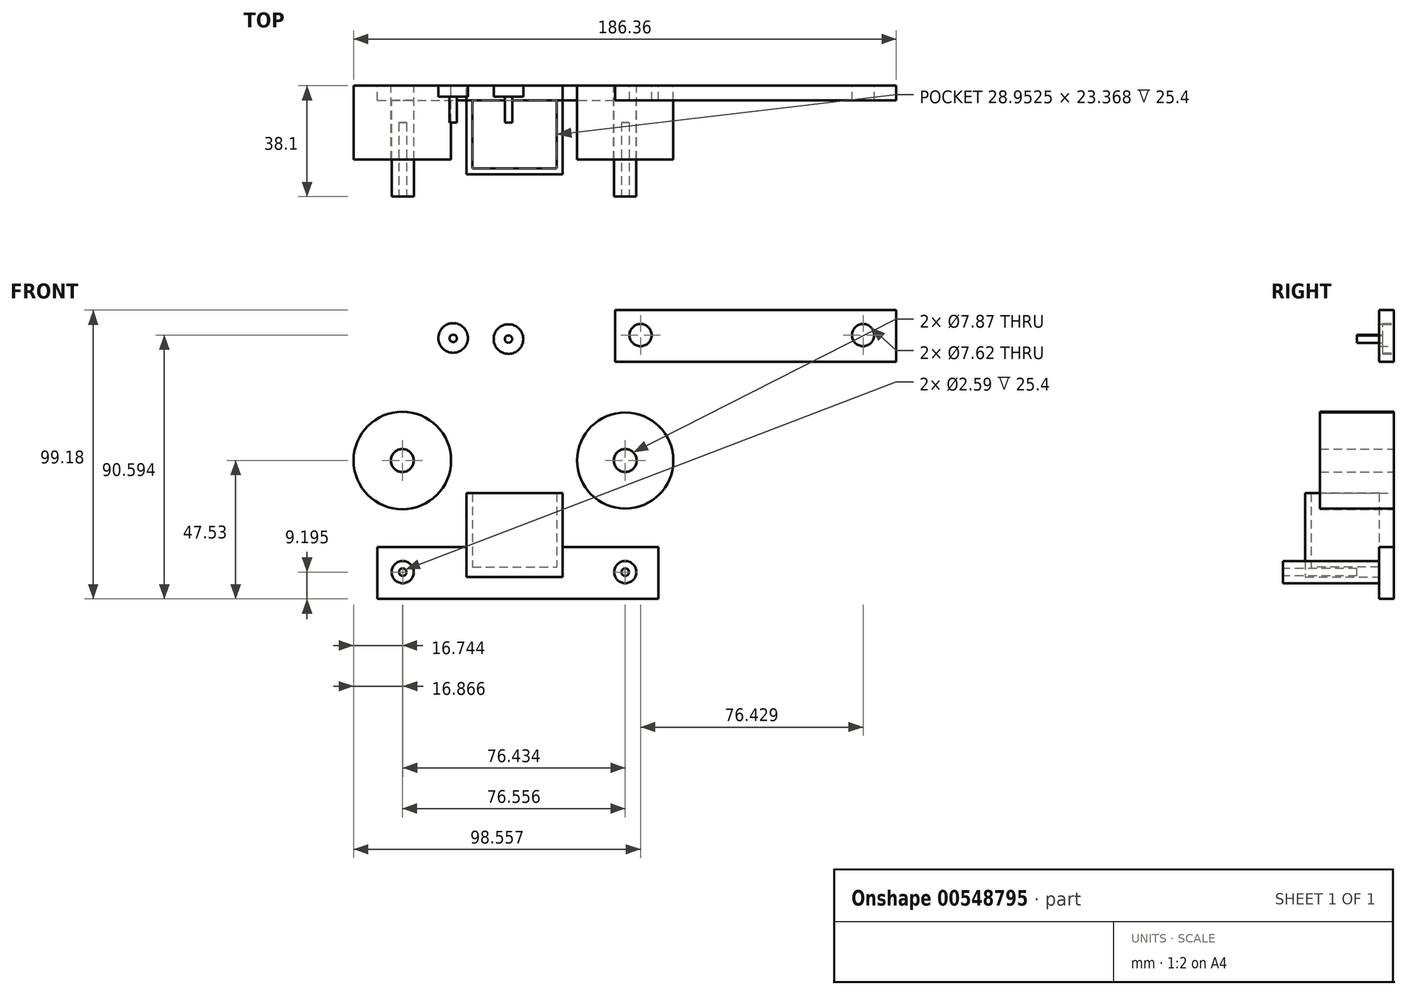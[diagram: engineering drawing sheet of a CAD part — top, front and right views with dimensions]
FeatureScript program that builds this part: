
annotation { "Feature Type Name" : "Feature", "Feature Type Description" : "" }
export const myFeature = defineFeature(function(context is Context, id is Id, definition is map)
    precondition{}
    {
        {
            var Q0;
            Q0=qCreatedBy(makeId("Front.planeOp"),FACE);
            var sketch = newSketch(context, id + "F0", { "sketchPlane" : qUnion([Q0])});
            skCircle(sketch, "E0", {"center": v(0, 0) * mm, "radius": 16.51 * mm});
            skCircle(sketch, "E1", {"center": v(0, 0) * mm, "radius": 3.94 * mm});
            skSolve(sketch);
        }
        {
            var Q0;
            Q0=makeQuery(id+"F0.imprint","IMPRINT",FACE,{"disambiguationData":[TD([[makeQuery(id+"F0.imprint","IMPRINT",EDGE,{"derivedFrom":sQuery(id+"F0.wireOp",EDGE,"E0")}),1.0]])]});
            extrude(context, id + "F1", {"entities" : qUnion([Q0]), "depth" : 25.4 * mm, "offsetDistance" : 25.4 * mm});
        }
        {
            var Q0;
            Q0=qCreatedBy(makeId("Front.planeOp"),FACE);
            var sketch = newSketch(context, id + "F2", { "sketchPlane" : qUnion([Q0])});
            skCircle(sketch, "E2", {"center": v(-76.56, 0) * mm, "radius": 16.74 * mm});
            skCircle(sketch, "E3", {"center": v(-76.56, 0) * mm, "radius": 3.94 * mm});
            skSolve(sketch);
        }
        {
            var Q0;
            Q0 = qSketchRegion(id + "F2", true);
            extrude(context, id + "F3", {"entities" : qUnion([Q0]), "depth" : 25.4 * mm, "offsetDistance" : 25.4 * mm});
        }
        {
            var Q0;
            Q0=qCreatedBy(makeId("Front.planeOp"),FACE);
            var sketch = newSketch(context, id + "F4", { "sketchPlane" : qUnion([Q0])});
            skCircle(sketch, "E4", {"center": v(0, -38.34) * mm, "radius": 3.81 * mm});
            skCircle(sketch, "E5", {"center": v(-76.43, -38.34) * mm, "radius": 3.81 * mm});
            skSolve(sketch);
        }
        {
            var Q0;
            Q0=qCreatedBy(makeId("Front.planeOp"),FACE);
            var sketch = newSketch(context, id + "F5", { "sketchPlane" : qUnion([Q0])});
            skLineSegment(sketch, "E6.bottom", {"start": v(-85.14, -29.75) * mm, "end": v(11.38, -29.75) * mm});
            skLineSegment(sketch, "E6.top", {"start": v(-85.14, -47.53) * mm, "end": v(11.38, -47.53) * mm});
            skLineSegment(sketch, "E6.left", {"start": v(-85.14, -29.75) * mm, "end": v(-85.14, -47.53) * mm});
            skLineSegment(sketch, "E6.right", {"start": v(11.38, -29.75) * mm, "end": v(11.38, -47.53) * mm});
            skSolve(sketch);
        }
        {
            var Q0;
            Q0=makeQuery(id+"F5.imprint","IMPRINT",FACE,{"disambiguationData":[TD([[makeQuery(id+"F5.imprint","IMPRINT",EDGE,{"derivedFrom":sQuery(id+"F5.wireOp",EDGE,"E6.bottom")}),-1.0]])]});
            extrude(context, id + "F6", {"entities" : qUnion([Q0]), "depth" : 5.08 * mm, "offsetDistance" : 25.4 * mm});
        }
        {
            var Q0;
            Q0=makeQuery(id+"F4.imprint","IMPRINT",FACE,{"disambiguationData":[TD([[makeQuery(id+"F4.imprint","IMPRINT",EDGE,{"derivedFrom":sQuery(id+"F4.wireOp",EDGE,"E4")}),1.0]])]});
            extrude(context, id + "F7", {"entities" : qUnion([Q0]), "operationType" : NewBodyOperationType.ADD, "depth" : 38.1 * mm, "offsetDistance" : 25.4 * mm});
        }
        {
            var Q0;
            Q0=makeQuery(id+"F4.imprint","IMPRINT",FACE,{"disambiguationData":[TD([[makeQuery(id+"F4.imprint","IMPRINT",EDGE,{"derivedFrom":sQuery(id+"F4.wireOp",EDGE,"E5")}),1.0]])]});
            extrude(context, id + "F8", {"entities" : qUnion([Q0]), "operationType" : NewBodyOperationType.ADD, "depth" : 38.1 * mm, "offsetDistance" : 25.4 * mm});
        }
        {
            var Q0;
            Q0=qCreatedBy(makeId("Front.planeOp"),FACE);
            var sketch = newSketch(context, id + "F9", { "sketchPlane" : qUnion([Q0])});
            skLineSegment(sketch, "E7.bottom", {"start": v(-3.46, 51.65) * mm, "end": v(93.06, 51.65) * mm});
            skLineSegment(sketch, "E7.top", {"start": v(-3.46, 33.87) * mm, "end": v(93.06, 33.87) * mm});
            skLineSegment(sketch, "E7.left", {"start": v(-3.46, 51.65) * mm, "end": v(-3.46, 33.87) * mm});
            skLineSegment(sketch, "E7.right", {"start": v(93.06, 51.65) * mm, "end": v(93.06, 33.87) * mm});
            skCircle(sketch, "E8", {"center": v(5.26, 43.06) * mm, "radius": 3.81 * mm});
            skCircle(sketch, "E9", {"center": v(81.69, 43.06) * mm, "radius": 3.81 * mm});
            skSolve(sketch);
        }
        {
            var Q0;
            Q0=makeQuery(id+"F9.imprint","IMPRINT",FACE,{"disambiguationData":[TD([[makeQuery(id+"F9.imprint","IMPRINT",EDGE,{"derivedFrom":sQuery(id+"F9.wireOp",EDGE,"E7.bottom")}),-1.0]])]});
            extrude(context, id + "F10", {"entities" : qUnion([Q0]), "depth" : 5.08 * mm, "offsetDistance" : 25.4 * mm});
        }
        {
            var Q0;
            Q0=qCreatedBy(makeId("Front.planeOp"),FACE);
            var sketch = newSketch(context, id + "F11", { "sketchPlane" : qUnion([Q0])});
            skCircle(sketch, "E10", {"center": v(-59.08, 41.95) * mm, "radius": 1.27 * mm});
            skSolve(sketch);
        }
        {
            var Q0;
            Q0 = qSketchRegion(id + "F11", true);
            extrude(context, id + "F12", {"entities" : qUnion([Q0]), "depth" : 12.7 * mm, "offsetDistance" : 25.4 * mm});
        }
        {
            var Q0;
            Q0=qCreatedBy(makeId("Front.planeOp"),FACE);
            var sketch = newSketch(context, id + "F13", { "sketchPlane" : qUnion([Q0])});
            skCircle(sketch, "E11", {"center": v(-59.12, 42.07) * mm, "radius": 5.08 * mm});
            skSolve(sketch);
        }
        {
            var Q0;
            Q0 = qSketchRegion(id + "F13", true);
            extrude(context, id + "F14", {"entities" : qUnion([Q0]), "operationType" : NewBodyOperationType.ADD, "depth" : 3.8 * mm, "offsetDistance" : 25.4 * mm});
        }
        {
            var Q0;
            Q0=makeQuery(id+"F6.opExtrude","CAP_FACE",FACE,{"disambiguationData":[OSD([sQuery(id+"F5.wireOp",EDGE,"E6.bottom"),sQuery(id+"F5.wireOp",EDGE,"E6.top"),sQuery(id+"F5.wireOp",EDGE,"E6.left"),sQuery(id+"F5.wireOp",EDGE,"E6.right")])],"isStart":false});
            var sketch = newSketch(context, id + "F15", { "sketchPlane" : qUnion([Q0])});
            skLineSegment(sketch, "E12.bottom", {"start": v(-54.5, -36.63) * mm, "end": v(-21.5, -36.63) * mm});
            skLineSegment(sketch, "E12.top", {"start": v(-54.5, -39.95) * mm, "end": v(-21.5, -39.95) * mm});
            skLineSegment(sketch, "E12.left", {"start": v(-54.5, -36.63) * mm, "end": v(-54.5, -39.95) * mm});
            skLineSegment(sketch, "E12.right", {"start": v(-21.5, -36.63) * mm, "end": v(-21.5, -39.95) * mm});
            skSolve(sketch);
        }
        {
            var Q0;
            Q0=makeQuery(id+"F15.imprint","IMPRINT",FACE,{"disambiguationData":[TD([[makeQuery(id+"F15.imprint","IMPRINT",EDGE,{"derivedFrom":sQuery(id+"F15.wireOp",EDGE,"E12.bottom")}),-1.0]])]});
            extrude(context, id + "F16", {"entities" : qUnion([Q0]), "operationType" : NewBodyOperationType.ADD, "depth" : 25.4 * mm, "offsetDistance" : 25.4 * mm});
        }
        {
            var Q0;
            Q0=makeQuery(id+"F8.opExtrude","CAP_FACE",FACE,{"disambiguationData":[OSD([sQuery(id+"F4.wireOp",EDGE,"E5")])],"isStart":false});
            var sketch = newSketch(context, id + "F17", { "sketchPlane" : qUnion([Q0])});
            skCircle(sketch, "E13", {"center": v(-76.43, -38.34) * mm, "radius": 1.3 * mm});
            skSolve(sketch);
        }
        {
            var Q0;
            Q0=makeQuery(id+"F17.imprint","IMPRINT",FACE,{"disambiguationData":[TD([[makeQuery(id+"F17.imprint","IMPRINT",EDGE,{"derivedFrom":sQuery(id+"F17.wireOp",EDGE,"E13")}),1.0]])]});
            extrude(context, id + "F18", {"entities" : qUnion([Q0]), "operationType" : NewBodyOperationType.REMOVE, "oppositeDirection" : true, "depth" : 25.4 * mm, "offsetDistance" : 25.4 * mm});
        }
        {
            var Q0;
            Q0=makeQuery(id+"F7.opExtrude","CAP_FACE",FACE,{"disambiguationData":[OSD([sQuery(id+"F4.wireOp",EDGE,"E4")])],"isStart":false});
            var sketch = newSketch(context, id + "F19", { "sketchPlane" : qUnion([Q0])});
            skCircle(sketch, "E14", {"center": v(0, -38.34) * mm, "radius": 1.3 * mm});
            skSolve(sketch);
        }
        {
            var Q0;
            Q0=makeQuery(id+"F19.imprint","IMPRINT",FACE,{"disambiguationData":[TD([[makeQuery(id+"F19.imprint","IMPRINT",EDGE,{"derivedFrom":sQuery(id+"F19.wireOp",EDGE,"E14")}),1.0]])]});
            extrude(context, id + "F20", {"entities" : qUnion([Q0]), "operationType" : NewBodyOperationType.REMOVE, "oppositeDirection" : true, "depth" : 25.4 * mm, "offsetDistance" : 25.4 * mm});
        }
        {
            var Q0;
            Q0=makeQuery(id+"F16.opExtrude","SWEPT_FACE",FACE,{"disambiguationData":[OSD([sQuery(id+"F15.wireOp",EDGE,"E12.bottom")])]});
            var sketch = newSketch(context, id + "F21", { "sketchPlane" : qUnion([Q0])});
            skLineSegment(sketch, "E15.bottom", {"start": v(-54.5, -5.08) * mm, "end": v(-52.48, -5.08) * mm});
            skLineSegment(sketch, "E15.top", {"start": v(-54.5, -30.48) * mm, "end": v(-52.48, -30.48) * mm});
            skLineSegment(sketch, "E15.left", {"start": v(-54.5, -5.08) * mm, "end": v(-54.5, -30.48) * mm});
            skLineSegment(sketch, "E15.right", {"start": v(-52.48, -5.08) * mm, "end": v(-52.48, -30.48) * mm});
            skLineSegment(sketch, "E16.bottom", {"start": v(-21.5, -30.48) * mm, "end": v(-23.53, -30.48) * mm});
            skLineSegment(sketch, "E16.top", {"start": v(-21.5, -5.08) * mm, "end": v(-23.53, -5.08) * mm});
            skLineSegment(sketch, "E16.left", {"start": v(-21.5, -30.48) * mm, "end": v(-21.5, -5.08) * mm});
            skLineSegment(sketch, "E16.right", {"start": v(-23.53, -30.48) * mm, "end": v(-23.53, -5.08) * mm});
            skSolve(sketch);
        }
        {
            var Q0;
            Q0=makeQuery(id+"F21.imprint","IMPRINT",FACE,{"disambiguationData":[TD([[makeQuery(id+"F21.imprint","IMPRINT",EDGE,{"derivedFrom":sQuery(id+"F21.wireOp",EDGE,"E15.bottom")}),-1.0]])]});
            extrude(context, id + "F22", {"entities" : qUnion([Q0]), "operationType" : NewBodyOperationType.ADD, "depth" : 25.4 * mm, "offsetDistance" : 25.4 * mm});
        }
        {
            var Q0;
            Q0=makeQuery(id+"F16.opExtrude","SWEPT_FACE",FACE,{"disambiguationData":[OSD([sQuery(id+"F15.wireOp",EDGE,"E12.bottom")])]});
            var sketch = newSketch(context, id + "F23", { "sketchPlane" : qUnion([Q0])});
            skLineSegment(sketch, "E17.bottom", {"start": v(-21.5, -30.48) * mm, "end": v(-23.53, -30.48) * mm});
            skLineSegment(sketch, "E17.top", {"start": v(-21.5, -5.08) * mm, "end": v(-23.53, -5.08) * mm});
            skLineSegment(sketch, "E17.left", {"start": v(-21.5, -30.48) * mm, "end": v(-21.5, -5.08) * mm});
            skLineSegment(sketch, "E17.right", {"start": v(-23.53, -30.48) * mm, "end": v(-23.53, -5.08) * mm});
            skSolve(sketch);
        }
        {
            var Q0;
            Q0=makeQuery(id+"F23.imprint","IMPRINT",FACE,{"disambiguationData":[TD([[makeQuery(id+"F23.imprint","IMPRINT",EDGE,{"derivedFrom":sQuery(id+"F23.wireOp",EDGE,"E17.bottom")}),1.0]])]});
            extrude(context, id + "F24", {"entities" : qUnion([Q0]), "operationType" : NewBodyOperationType.ADD, "depth" : 25.4 * mm, "offsetDistance" : 25.4 * mm});
        }
        {
            var Q0;
            Q0=makeQuery(id+"F16.opExtrude","SWEPT_FACE",FACE,{"disambiguationData":[OSD([sQuery(id+"F15.wireOp",EDGE,"E12.bottom")])]});
            var sketch = newSketch(context, id + "F25", { "sketchPlane" : qUnion([Q0])});
            skLineSegment(sketch, "E18.bottom", {"start": v(-52.48, -30.48) * mm, "end": v(-23.53, -30.48) * mm});
            skLineSegment(sketch, "E18.top", {"start": v(-52.48, -28.45) * mm, "end": v(-23.53, -28.45) * mm});
            skLineSegment(sketch, "E18.left", {"start": v(-52.48, -30.48) * mm, "end": v(-52.48, -28.45) * mm});
            skLineSegment(sketch, "E18.right", {"start": v(-23.53, -30.48) * mm, "end": v(-23.53, -28.45) * mm});
            skSolve(sketch);
        }
        {
            var Q0;
            Q0=makeQuery(id+"F25.imprint","IMPRINT",FACE,{"disambiguationData":[TD([[makeQuery(id+"F25.imprint","IMPRINT",EDGE,{"derivedFrom":sQuery(id+"F25.wireOp",EDGE,"E18.bottom")}),1.0]])]});
            extrude(context, id + "F26", {"entities" : qUnion([Q0]), "operationType" : NewBodyOperationType.ADD, "depth" : 25.4 * mm, "offsetDistance" : 25.4 * mm});
        }
        {
            var Q0;
            Q0=makeQuery(id+"F6.opExtrude","SWEPT_FACE",FACE,{"disambiguationData":[OSD([sQuery(id+"F5.wireOp",EDGE,"E6.bottom")])]});
            var sketch = newSketch(context, id + "F27", { "sketchPlane" : qUnion([Q0])});
            skLineSegment(sketch, "E19.bottom", {"start": v(-21.5, -5.08) * mm, "end": v(-54.5, -5.08) * mm});
            skLineSegment(sketch, "E19.top", {"start": v(-21.5, 0) * mm, "end": v(-54.5, 0) * mm});
            skLineSegment(sketch, "E19.left", {"start": v(-21.5, -5.08) * mm, "end": v(-21.5, 0) * mm});
            skLineSegment(sketch, "E19.right", {"start": v(-54.5, -5.08) * mm, "end": v(-54.5, 0) * mm});
            skSolve(sketch);
        }
        {
            var Q0;
            Q0=makeQuery(id+"F27.imprint","IMPRINT",FACE,{"disambiguationData":[TD([[makeQuery(id+"F27.imprint","IMPRINT",EDGE,{"derivedFrom":sQuery(id+"F27.wireOp",EDGE,"E19.top")}),-1.0]])]});
            extrude(context, id + "F28", {"entities" : qUnion([Q0]), "operationType" : NewBodyOperationType.ADD, "depth" : 18.54 * mm, "offsetDistance" : 25.4 * mm});
        }
        {
            var Q0;
            Q0=makeQuery(id+"FQeDFR8k07Q3g6k_8.opExtrude","CAP_FACE",FACE,{"disambiguationData":[OSD([sQuery(id+"FtJ5DPthQIBCUxf_8.wireOp",EDGE,"swfkERgy-3qCU-8dWv-s7Tl-giiPDrWiPdEZ")])],"isStart":false});
            var sketch = newSketch(context, id + "F29", { "sketchPlane" : qUnion([Q0])});
            skSolve(sketch);
        }
        {
            var Q0;
            Q0=qCreatedBy(makeId("Front.planeOp"),FACE);
            var sketch = newSketch(context, id + "F30", { "sketchPlane" : qUnion([Q0])});
            skCircle(sketch, "E20", {"center": v(-40.1, 41.71) * mm, "radius": 5.08 * mm});
            skCircle(sketch, "E21", {"center": v(-40.1, 41.71) * mm, "radius": 1.27 * mm});
            skSolve(sketch);
        }
        {
            var Q0;
            Q0=makeQuery(id+"F30.imprint","IMPRINT",FACE,{"disambiguationData":[TD([[makeQuery(id+"F30.imprint","IMPRINT",EDGE,{"derivedFrom":sQuery(id+"F30.wireOp",EDGE,"E20")}),1.0]])]});
            extrude(context, id + "F31", {"entities" : qUnion([Q0]), "depth" : 3.8 * mm, "offsetDistance" : 25.4 * mm});
        }
        {
            var Q0;
            Q0=makeQuery(id+"F30.imprint","IMPRINT",FACE,{"disambiguationData":[TD([[makeQuery(id+"F30.imprint","IMPRINT",EDGE,{"derivedFrom":sQuery(id+"F30.wireOp",EDGE,"E21")}),1.0]])]});
            extrude(context, id + "F32", {"entities" : qUnion([Q0]), "operationType" : NewBodyOperationType.ADD, "depth" : 12.7 * mm, "offsetDistance" : 25.4 * mm});
        }
    });
